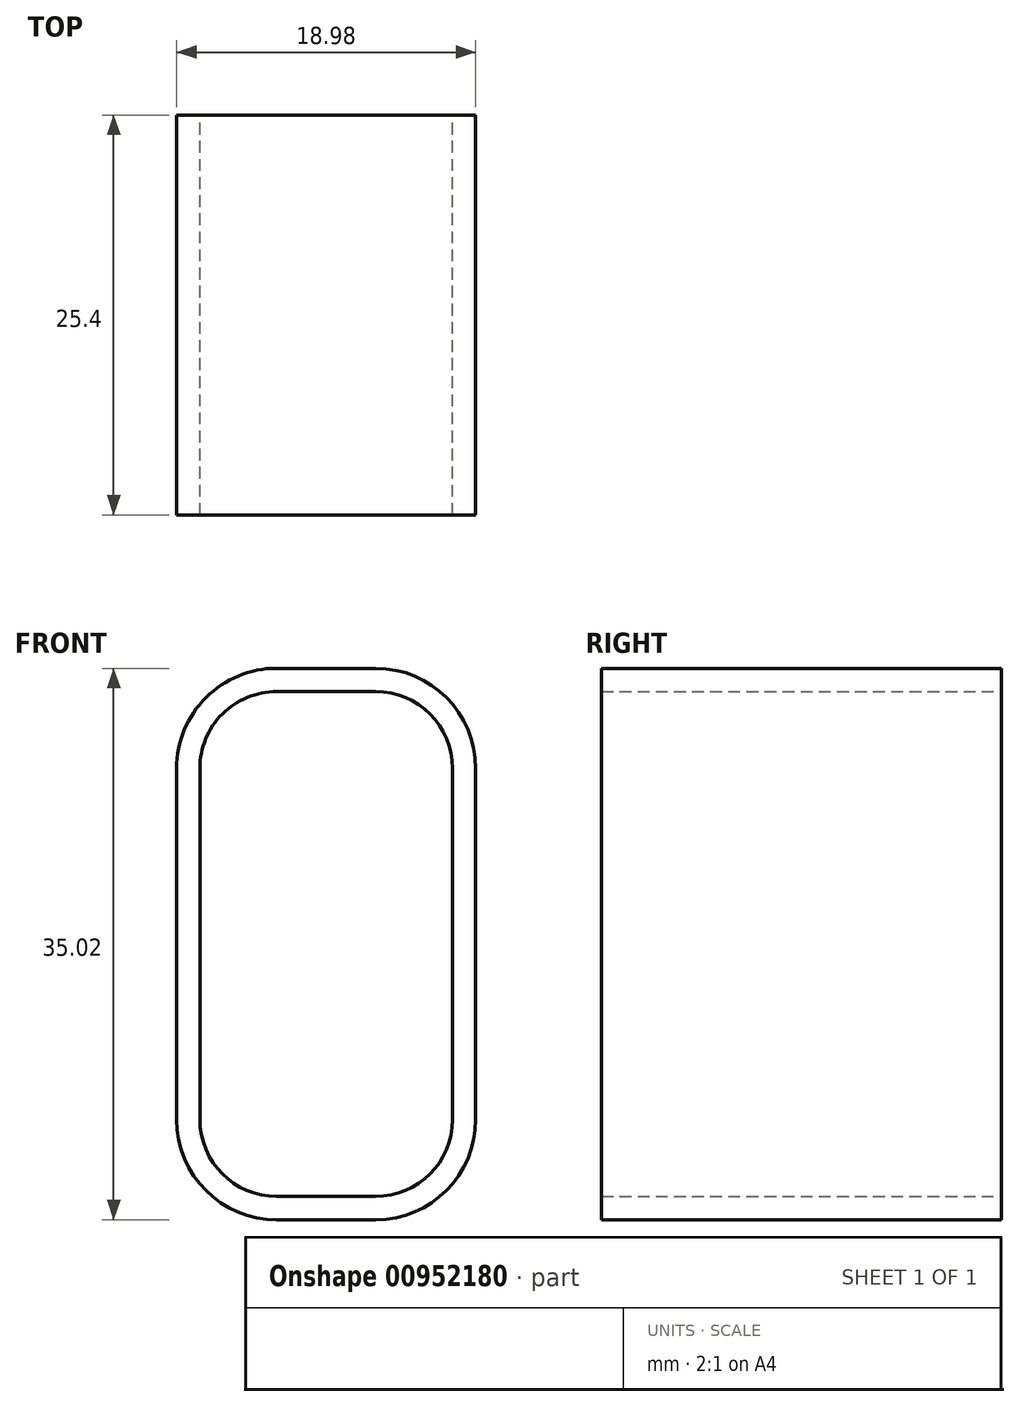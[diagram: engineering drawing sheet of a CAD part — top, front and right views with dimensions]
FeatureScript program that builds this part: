
annotation { "Feature Type Name" : "Feature", "Feature Type Description" : "" }
export const myFeature = defineFeature(function(context is Context, id is Id, definition is map)
    precondition{}
    {
        {
            var Q0;
            Q0=qCreatedBy(makeId("Front.planeOp"),FACE);
            var sketch = newSketch(context, id + "F0", { "sketchPlane" : qUnion([Q0])});
            skLineSegment(sketch, "E0.bottom", {"start": v(3.14, -16.04) * mm, "end": v(-3.14, -16.04) * mm});
            skLineSegment(sketch, "E0.top", {"start": v(3.14, 16.04) * mm, "end": v(-3.14, 16.04) * mm});
            skLineSegment(sketch, "E0.left", {"start": v(8.02, -11.16) * mm, "end": v(8.02, 11.16) * mm});
            skLineSegment(sketch, "E0.right", {"start": v(-8.02, -11.16) * mm, "end": v(-8.02, 11.16) * mm});
            skPoint(sketch, "E0.middle", {"position": v(0, 0) * mm});
            skLineSegment(sketch, "E1.0", {"start": v(3.14, -17.51) * mm, "end": v(-3.14, -17.51) * mm});
            skLineSegment(sketch, "E1.1", {"start": v(9.5, -11.16) * mm, "end": v(9.5, 11.16) * mm});
            skLineSegment(sketch, "E1.2", {"start": v(3.14, 17.51) * mm, "end": v(-3.14, 17.51) * mm});
            skLineSegment(sketch, "E1.3", {"start": v(-9.5, -11.16) * mm, "end": v(-9.5, 11.16) * mm});
            skPoint(sketch, "E2.visualSharp", {"position": v(-8.02, 16.04) * mm});
            skArc(sketch, "E2.filletArc", {"start": v(-3.14, 16.04) * mm, "mid": v(-6.6, 14.61) * mm, "end": v(-8.02, 11.16) * mm});
            skPoint(sketch, "E3.visualSharp", {"position": v(8.02, 16.04) * mm});
            skArc(sketch, "E3.filletArc", {"start": v(8.02, 11.16) * mm, "mid": v(6.6, 14.61) * mm, "end": v(3.14, 16.04) * mm});
            skPoint(sketch, "E4.visualSharp", {"position": v(8.02, -16.04) * mm});
            skArc(sketch, "E4.filletArc", {"start": v(3.14, -16.04) * mm, "mid": v(6.6, -14.61) * mm, "end": v(8.02, -11.16) * mm});
            skPoint(sketch, "E5.visualSharp", {"position": v(-8.02, -16.04) * mm});
            skArc(sketch, "E5.filletArc", {"start": v(-8.02, -11.16) * mm, "mid": v(-6.6, -14.61) * mm, "end": v(-3.14, -16.04) * mm});
            skPoint(sketch, "E6.visualSharp", {"position": v(-9.5, 17.51) * mm});
            skArc(sketch, "E6.filletArc", {"start": v(-3.14, 17.51) * mm, "mid": v(-7.63, 15.65) * mm, "end": v(-9.5, 11.16) * mm});
            skPoint(sketch, "E7.visualSharp", {"position": v(9.5, 17.51) * mm});
            skArc(sketch, "E7.filletArc", {"start": v(9.5, 11.16) * mm, "mid": v(7.63, 15.65) * mm, "end": v(3.14, 17.51) * mm});
            skPoint(sketch, "E8.visualSharp", {"position": v(9.5, -17.51) * mm});
            skArc(sketch, "E8.filletArc", {"start": v(3.14, -17.51) * mm, "mid": v(7.63, -15.65) * mm, "end": v(9.5, -11.16) * mm});
            skPoint(sketch, "E9.visualSharp", {"position": v(-9.5, -17.51) * mm});
            skArc(sketch, "E9.filletArc", {"start": v(-9.5, -11.16) * mm, "mid": v(-7.63, -15.65) * mm, "end": v(-3.14, -17.51) * mm});
            skSolve(sketch);
        }
        {
            var Q0;
            Q0 = qSketchRegion(id + "F0", true);
            extrude(context, id + "F1", {"entities" : qUnion([Q0]), "depth" : 25.4 * mm, "offsetDistance" : 25.4 * mm});
        }
    });
